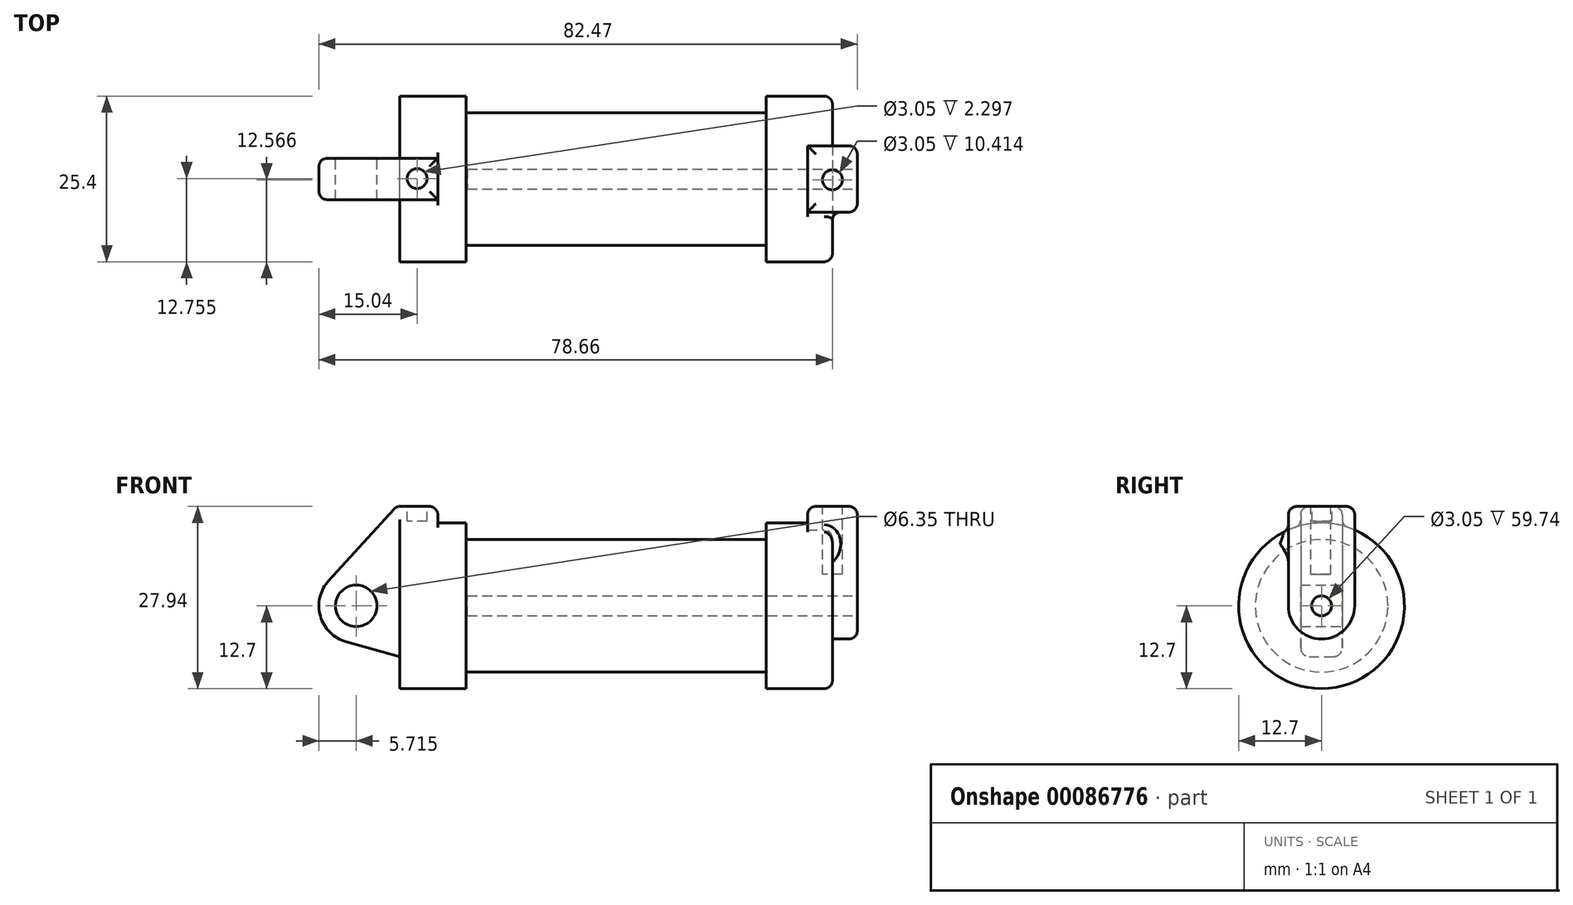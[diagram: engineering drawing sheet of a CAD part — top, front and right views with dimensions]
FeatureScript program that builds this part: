
annotation { "Feature Type Name" : "Feature", "Feature Type Description" : "" }
export const myFeature = defineFeature(function(context is Context, id is Id, definition is map)
    precondition{}
    {
        {
            var Q0;
            Q0=qCreatedBy(makeId("Front.planeOp"),FACE);
            var sketch = newSketch(context, id + "F0", { "sketchPlane" : qUnion([Q0])});
            skLineSegment(sketch, "E0", {"start": v(0, 0) * mm, "end": v(0, 12.7) * mm});
            skLineSegment(sketch, "E1", {"start": v(0, 12.7) * mm, "end": v(10.16, 12.7) * mm});
            skLineSegment(sketch, "E2", {"start": v(10.16, 12.7) * mm, "end": v(10.16, 10.16) * mm});
            skLineSegment(sketch, "E3", {"start": v(10.16, 10.16) * mm, "end": v(56.13, 10.16) * mm});
            skLineSegment(sketch, "E4", {"start": v(56.13, 10.16) * mm, "end": v(56.13, 12.7) * mm});
            skLineSegment(sketch, "E5", {"start": v(56.13, 12.7) * mm, "end": v(66.3, 12.7) * mm});
            skLineSegment(sketch, "E6", {"start": v(66.3, 12.7) * mm, "end": v(66.3, 0) * mm});
            skLineSegment(sketch, "E7", {"start": v(66.3, 0) * mm, "end": v(0, 0) * mm});
            skLineSegment(sketch, "E8", {"start": v(5.84, 15.24) * mm, "end": v(-0.5, 15.24) * mm});
            skLineSegment(sketch, "E9", {"start": v(-0.5, 15.24) * mm, "end": v(-10.88, 3.85) * mm});
            skLineSegment(sketch, "E10", {"start": v(0, 0) * mm, "end": v(-6.65, 0) * mm});
            skCircle(sketch, "E11", {"center": v(-6.65, 0) * mm, "radius": 5.72 * mm});
            skCircle(sketch, "E12", {"center": v(-6.65, 0) * mm, "radius": 3.18 * mm});
            skLineSegment(sketch, "E13", {"start": v(5.84, 15.24) * mm, "end": v(5.84, -9.4) * mm});
            skLineSegment(sketch, "E14", {"start": v(5.84, -9.4) * mm, "end": v(-8.18, -5.5) * mm});
            skSolve(sketch);
        }
        {
            var Q0;
            {var subQ0=sQuery(id+"F0.wireOp",EDGE,"E2");Q0=makeQuery(id+"F0.imprint","IMPRINT",FACE,{"disambiguationData":[TD([[makeQuery(id+"F0.imprint","IMPRINT",EDGE,{"derivedFrom":subQ0}),-1.0]])]});}
            var Q1;
            {var subQ0=sQuery(id+"F0.wireOp",EDGE,"E0");Q1=makeQuery(id+"F0.imprint","IMPRINT",FACE,{"disambiguationData":[TD([[makeQuery(id+"F0.imprint","IMPRINT",EDGE,{"derivedFrom":subQ0}),-1.0]])]});}
            var Q2;
            Q2=sQuery(id+"F0.wireOp",EDGE,"E10");
            revolve(context, id + "F1", {"entities" : qUnion([Q0, Q1]), "axis" : qUnion([Q2]), "revolveType" : RevolveType.FULL});
        }
        {
            var Q0;
            {var subQ4=sQuery(id+"F0.wireOp",EDGE,"E12");Q0=makeQuery(id+"F0.imprint","IMPRINT",FACE,{"disambiguationData":[TD([[makeQuery(id+"F0.imprint","IMPRINT",EDGE,{"derivedFrom":subQ4}),-1.0]])]});}
            var Q1;
            {var subQ3=sQuery(id+"F0.wireOp",EDGE,"E0");Q1=makeQuery(id+"F0.imprint","IMPRINT",FACE,{"disambiguationData":[TD([[makeQuery(id+"F0.imprint","IMPRINT",EDGE,{"derivedFrom":subQ3}),1.0]])]});}
            var Q2;
            {var subQ0=sQuery(id+"F0.wireOp",EDGE,"E14");Q2=makeQuery(id+"F0.imprint","IMPRINT",FACE,{"disambiguationData":[TD([[makeQuery(id+"F0.imprint","IMPRINT",EDGE,{"derivedFrom":subQ0}),-1.0]])]});}
            var Q3;
            {var subQ0=sQuery(id+"F0.wireOp",EDGE,"E0");Q3=makeQuery(id+"F0.imprint","IMPRINT",FACE,{"disambiguationData":[TD([[makeQuery(id+"F0.imprint","IMPRINT",EDGE,{"derivedFrom":subQ0}),-1.0]])]});}
            extrude(context, id + "F2", {"entities" : qUnion([Q0, Q1, Q2, Q3]), "operationType" : NewBodyOperationType.ADD, "endBound" : BoundingType.SYMMETRIC, "depth" : 6.35 * mm});
        }
        {
            var Q0;
            Q0=makeQuery(id+"F1.opRevolve","SWEPT_FACE",FACE,{"disambiguationData":[OSD([sQuery(id+"F0.wireOp",EDGE,"E6")])]});
            var sketch = newSketch(context, id + "F3", { "sketchPlane" : qUnion([Q0])});
            skCircle(sketch, "E15", {"center": v(0, 0) * mm, "radius": 1.52 * mm});
            skCircle(sketch, "E16", {"center": v(0, 0) * mm, "radius": 5.08 * mm});
            skPoint(sketch, "E17", {"position": v(-5.08, 0) * mm});
            skPoint(sketch, "E18", {"position": v(5.08, 0) * mm});
            skLineSegment(sketch, "E19", {"start": v(-5.08, 0) * mm, "end": v(-5.08, 15.24) * mm});
            skLineSegment(sketch, "E20", {"start": v(5.08, 15.24) * mm, "end": v(5.08, 0) * mm});
            skLineSegment(sketch, "E21", {"start": v(-5.08, 15.24) * mm, "end": v(5.08, 15.24) * mm});
            skSolve(sketch);
        }
        {
            var Q0;
            Q0=makeQuery(id+"F3.imprint","IMPRINT",FACE,{"disambiguationData":[TD([[makeQuery(id+"F3.imprint","IMPRINT",EDGE,{"derivedFrom":sQuery(id+"F3.wireOp",EDGE,"E15")}),1.0]])]});
            var Q1;
            {var subQ0=sQuery(id+"F3.wireOp",EDGE,"E19");var subQ1=sQuery(id+"F3.wireOp",EDGE,"E16");var subQ2=makeQuery(id+"F3.imprint","INTERSECT",VERTEX,{"derivedFrom":[subQ1,subQ0]});Q1=makeQuery(id+"F3.imprint","IMPRINT",FACE,{"disambiguationData":[TD([[makeQuery(id+"F3.imprint","IMPRINT",EDGE,{"disambiguationData":[TD([[subQ2,1.0]])],"derivedFrom":subQ1}),-1.0]])]});}
            var Q2;
            {var subQ0=sQuery(id+"F3.wireOp",EDGE,"E21");Q2=makeQuery(id+"F3.imprint","IMPRINT",FACE,{"disambiguationData":[TD([[makeQuery(id+"F3.imprint","IMPRINT",EDGE,{"derivedFrom":subQ0}),-1.0]])]});}
            var Q3;
            Q3=makeQuery(id+"F3.imprint","IMPRINT",FACE,{"disambiguationData":[TD([[makeQuery(id+"F3.imprint","IMPRINT",EDGE,{"derivedFrom":sQuery(id+"F3.wireOp",EDGE,"E15")}),-1.0]])]});
            extrude(context, id + "F4", {"entities" : qUnion([Q0, Q1, Q2, Q3]), "operationType" : NewBodyOperationType.ADD, "endBound" : BoundingType.SYMMETRIC, "oppositeDirection" : true, "depth" : 7.62 * mm});
        }
        {
            var Q0;
            Q0=makeQuery(id+"F4.opExtrude","CAP_FACE",FACE,{"disambiguationData":[OSD([sQuery(id+"F3.wireOp",EDGE,"E16"),sQuery(id+"F3.wireOp",EDGE,"E19"),sQuery(id+"F3.wireOp",EDGE,"E20"),sQuery(id+"F3.wireOp",EDGE,"E21")])],"isStart":true});
            var sketch = newSketch(context, id + "F5", { "sketchPlane" : qUnion([Q0])});
            skCircle(sketch, "E22", {"center": v(0, 0) * mm, "radius": 1.52 * mm});
            skSolve(sketch);
        }
        {
            var Q0;
            Q0=makeQuery(id+"F5.imprint","IMPRINT",FACE,{"disambiguationData":[TD([[makeQuery(id+"F5.imprint","IMPRINT",EDGE,{"derivedFrom":sQuery(id+"F5.wireOp",EDGE,"E22")}),1.0]])]});
            var Q1;
            Q1=sQuery(id+"F5.wireOp",EDGE,"E22");
            extrude(context, id + "F6", {"entities" : qUnion([Q0]), "operationType" : NewBodyOperationType.REMOVE, "surfaceEntities" : qUnion([Q1]), "oppositeDirection" : true, "depth" : 59.74 * mm});
        }
        {
            var Q0;
            Q0=makeQuery(id+"F2.opExtrude","SWEPT_FACE",FACE,{"disambiguationData":[OSD([sQuery(id+"F0.wireOp",EDGE,"E8")])]});
            var sketch = newSketch(context, id + "F7", { "sketchPlane" : qUnion([Q0])});
            skCircle(sketch, "E23", {"center": v(2.67, 0.05) * mm, "radius": 1.52 * mm});
            skSolve(sketch);
        }
        {
            var Q0;
            Q0=makeQuery(id+"F7.imprint","IMPRINT",FACE,{"disambiguationData":[TD([[makeQuery(id+"F7.imprint","IMPRINT",EDGE,{"derivedFrom":sQuery(id+"F7.wireOp",EDGE,"E23")}),1.0]])]});
            extrude(context, id + "F8", {"entities" : qUnion([Q0]), "operationType" : NewBodyOperationType.REMOVE, "oppositeDirection" : true, "depth" : 2.3 * mm});
        }
        {
            var Q0;
            Q0=makeQuery(id+"F4.opExtrude","SWEPT_FACE",FACE,{"disambiguationData":[OSD([sQuery(id+"F3.wireOp",EDGE,"E21")])]});
            var sketch = newSketch(context, id + "F9", { "sketchPlane" : qUnion([Q0])});
            skCircle(sketch, "E24", {"center": v(66.29, -0.13) * mm, "radius": 1.52 * mm});
            skSolve(sketch);
        }
        {
            var Q0;
            Q0=makeQuery(id+"F9.imprint","IMPRINT",FACE,{"disambiguationData":[TD([[makeQuery(id+"F9.imprint","IMPRINT",EDGE,{"derivedFrom":sQuery(id+"F9.wireOp",EDGE,"E24")}),1.0]])]});
            extrude(context, id + "F10", {"entities" : qUnion([Q0]), "operationType" : NewBodyOperationType.REMOVE, "oppositeDirection" : true, "depth" : 10.4 * mm});
        }
        {
            var Q0;
            Q0=makeQuery(id+"F2.opExtrude","CAP_EDGE",EDGE,{"disambiguationData":[OSD([sQuery(id+"F0.wireOp",EDGE,"E8")])],"isStart":true});
            var Q1;
            Q1=makeQuery(id+"F2.opExtrude","SWEPT_EDGE",EDGE,{"disambiguationData":[OSD([sQuery(id+"F0.wireOp",EDGE,"E8"),sQuery(id+"F0.wireOp",EDGE,"E13")])]});
            var Q2;
            Q2=makeQuery(id+"F2.opExtrude","CAP_EDGE",EDGE,{"disambiguationData":[OSD([sQuery(id+"F0.wireOp",EDGE,"E8")])],"isStart":false});
            var Q3;
            Q3=makeQuery(id+"F2.opExtrude","SWEPT_EDGE",EDGE,{"disambiguationData":[OSD([sQuery(id+"F0.wireOp",EDGE,"E8"),sQuery(id+"F0.wireOp",EDGE,"E9")])]});
            var Q4;
            Q4=makeQuery(id+"F2.opExtrude","CAP_EDGE",EDGE,{"disambiguationData":[OSD([sQuery(id+"F0.wireOp",EDGE,"E9")])],"isStart":false});
            var Q5;
            Q5=makeQuery(id+"F2.opExtrude","CAP_EDGE",EDGE,{"disambiguationData":[OSD([sQuery(id+"F0.wireOp",EDGE,"E9")])],"isStart":true});
            var Q6;
            Q6=makeQuery(id+"F2.boolean.opBoolean","INTERSECT",EDGE,{"derivedFrom":[makeQuery(id+"F1.opRevolve","SWEPT_FACE",FACE,{"disambiguationData":[OSD([sQuery(id+"F0.wireOp",EDGE,"E1")])]}),makeQuery(id+"F2.opExtrude","CAP_FACE",FACE,{"disambiguationData":[OSD([sQuery(id+"F0.wireOp",EDGE,"E8"),sQuery(id+"F0.wireOp",EDGE,"E9"),sQuery(id+"F0.wireOp",EDGE,"E11"),sQuery(id+"F0.wireOp",EDGE,"E12"),sQuery(id+"F0.wireOp",EDGE,"E13"),sQuery(id+"F0.wireOp",EDGE,"E14")])],"isStart":true})]});
            var Q7;
            Q7=makeQuery(id+"F2.boolean.opBoolean","INTERSECT",EDGE,{"derivedFrom":[makeQuery(id+"F1.opRevolve","SWEPT_FACE",FACE,{"disambiguationData":[OSD([sQuery(id+"F0.wireOp",EDGE,"E1")])]}),makeQuery(id+"F2.opExtrude","CAP_FACE",FACE,{"disambiguationData":[OSD([sQuery(id+"F0.wireOp",EDGE,"E8"),sQuery(id+"F0.wireOp",EDGE,"E9"),sQuery(id+"F0.wireOp",EDGE,"E11"),sQuery(id+"F0.wireOp",EDGE,"E12"),sQuery(id+"F0.wireOp",EDGE,"E13"),sQuery(id+"F0.wireOp",EDGE,"E14")])],"isStart":false})]});
            fillet(context, id + "F11", {"entities" : qUnion([Q0, Q1, Q2, Q3, Q4, Q5, Q6, Q7]), "radius" : 1.27 * mm, "tangentPropagation" : true, "allowEdgeOverflow" : false});
        }
        {
            var Q0;
            Q0=makeQuery(id+"F4.opExtrude","CAP_EDGE",EDGE,{"disambiguationData":[OSD([sQuery(id+"F3.wireOp",EDGE,"E21")])],"isStart":false});
            var Q1;
            Q1=makeQuery(id+"F4.opExtrude","SWEPT_EDGE",EDGE,{"disambiguationData":[OSD([sQuery(id+"F3.wireOp",EDGE,"E20"),sQuery(id+"F3.wireOp",EDGE,"E21")])]});
            var Q2;
            Q2=makeQuery(id+"F4.opExtrude","CAP_EDGE",EDGE,{"disambiguationData":[OSD([sQuery(id+"F3.wireOp",EDGE,"E21")])],"isStart":true});
            var Q3;
            Q3=makeQuery(id+"F4.opExtrude","SWEPT_EDGE",EDGE,{"disambiguationData":[OSD([sQuery(id+"F3.wireOp",EDGE,"E19"),sQuery(id+"F3.wireOp",EDGE,"E21")])]});
            var Q4;
            Q4=makeQuery(id+"F4.opExtrude","CAP_EDGE",EDGE,{"disambiguationData":[OSD([sQuery(id+"F3.wireOp",EDGE,"E20")])],"isStart":true});
            var Q5;
            Q5=makeQuery(id+"F4.boolean.opBoolean","INTERSECT",EDGE,{"derivedFrom":[makeQuery(id+"F1.opRevolve","SWEPT_FACE",FACE,{"disambiguationData":[OSD([sQuery(id+"F0.wireOp",EDGE,"E5")])]}),makeQuery(id+"F4.opExtrude","SWEPT_FACE",FACE,{"disambiguationData":[OSD([sQuery(id+"F3.wireOp",EDGE,"E19")])]})]});
            var Q6;
            Q6=makeQuery(id+"F1.opRevolve","SWEPT_EDGE",EDGE,{"disambiguationData":[OSD([sQuery(id+"F0.wireOp",EDGE,"E5"),sQuery(id+"F0.wireOp",EDGE,"E6")])]});
            fillet(context, id + "F12", {"entities" : qUnion([Q0, Q1, Q2, Q3, Q4, Q5, Q6]), "radius" : 1.27 * mm, "tangentPropagation" : true, "allowEdgeOverflow" : false});
        }
    });
